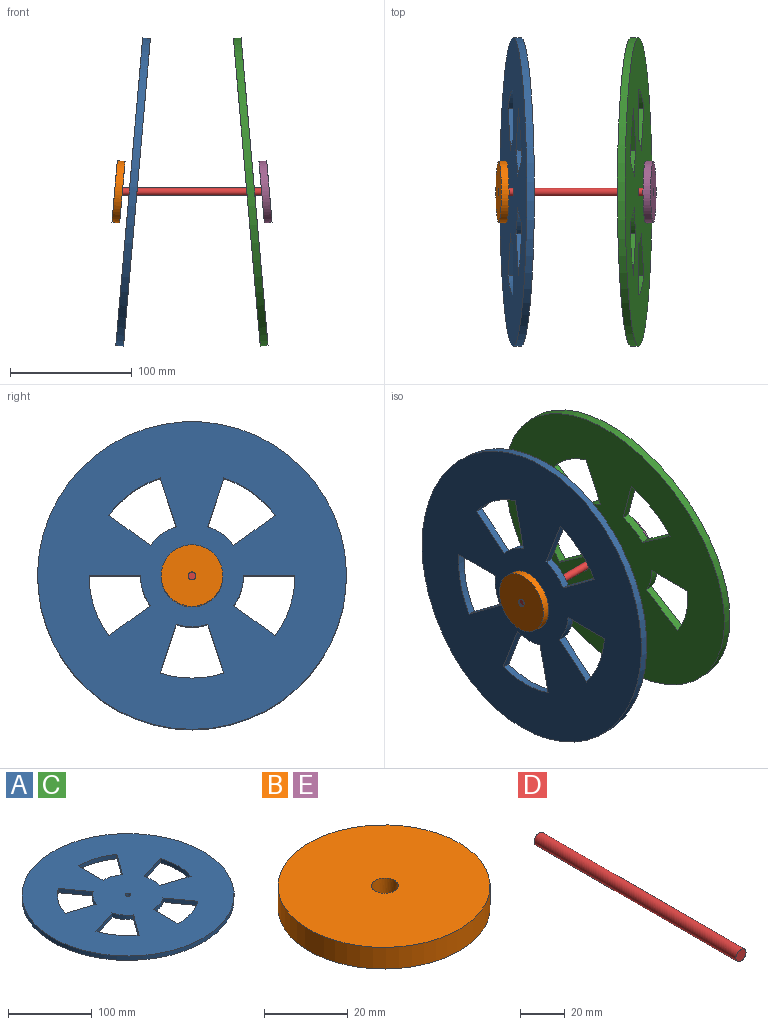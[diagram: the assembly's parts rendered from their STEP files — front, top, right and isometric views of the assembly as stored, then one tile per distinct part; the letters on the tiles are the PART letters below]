
ASSEMBLY  parts=5 mates=4
PART A: 24 faces, bbox 254x254x7.5 mm
  f0: plane 40.26x13.08mm, normal (0.31,0.95,0), area 268.8mm2, adj f1,f20,f21,f22
  f1: cylinder r=42.33mm len=26.16mm, axis (0,0,1), area 168.9mm2, adj f0,f2,f21,f22
  f2: plane 40.26x13.08mm, normal (0.31,-0.95,0), area 268.8mm2, adj f1,f20,f21,f22
  f3: plane 42.33x6.35mm, normal (1,0,0), area 268.8mm2, adj f4,f15,f21,f22
  f4: cylinder r=42.33mm len=24.88mm, axis (0,0,1), area 168.9mm2, adj f3,f5,f21,f22
  f5: plane 34.25x24.88mm, normal (-0.81,-0.59,0), area 268.8mm2, adj f4,f15,f21,f22
  f6: plane 40.26x13.08mm, normal (0.31,-0.95,0), area 268.8mm2, adj f7,f16,f21,f22
  f7: cylinder r=42.33mm len=21.17mm, axis (0,0,1), area 168.9mm2, adj f6,f8,f21,f22
  f8: plane 34.25x24.88mm, normal (-0.81,0.59,0), area 268.8mm2, adj f7,f16,f21,f22
  f9: plane 34.25x24.88mm, normal (-0.81,-0.59,0), area 268.8mm2, adj f10,f17,f21,f22
  f10: cylinder r=42.33mm len=21.17mm, axis (0,0,1), area 168.9mm2, adj f9,f11,f21,f22
  f11: plane 40.26x13.08mm, normal (0.31,0.95,0), area 268.8mm2, adj f10,f17,f21,f22
  f12: plane 42.33x6.35mm, normal (1,0,0), area 268.8mm2, adj f13,f19,f21,f22
  f13: cylinder r=84.67mm len=49.77mm, axis (0,0,1), area 337.8mm2, adj f12,f14,f21,f22
  f14: plane 34.25x24.88mm, normal (-0.81,0.59,0), area 268.8mm2, adj f13,f19,f21,f22
  f15: cylinder r=84.67mm len=49.77mm, axis (0,0,1), area 337.8mm2, adj f3,f5,f21,f22
  f16: cylinder r=84.67mm len=42.33mm, axis (0,0,1), area 337.8mm2, adj f6,f8,f21,f22
  f17: cylinder r=84.67mm len=42.33mm, axis (0,0,1), area 337.8mm2, adj f9,f11,f21,f22
  f18: cylinder r=127mm len=254mm, axis (0,0,1), area 5067.1mm2, adj f21,f22
  f19: cylinder r=42.33mm len=24.88mm, axis (0,0,1), area 168.9mm2, adj f12,f14,f21,f22
  f20: cylinder r=84.67mm len=52.33mm, axis (0,0,1), area 337.8mm2, adj f0,f2,f21,f22
  f21: plane 254x254mm, normal (0,0,-1), area 42193.8mm2, adj f0,f1,f2,f3,f4,f5,f6,f7
  f22: plane 254x254mm, normal (0,0,1), area 42193.8mm2, adj f0,f1,f2,f3,f4,f5,f6,f7
  f23: cylinder r=3.17mm len=7.46mm, axis (0.09,0,1), area 127.2mm2, adj f21,f22
PART B: 4 faces, bbox 50.8x50.8x7.5 mm
  f0: cylinder r=25.4mm len=50.8mm, axis (0,0,1), area 1013.4mm2, adj f1,f2
  f1: plane 50.8x50.8mm, normal (0,0,-1), area 1995mm2, adj f0,f3
  f2: plane 50.8x50.8mm, normal (0,0,1), area 1995mm2, adj f0,f3
  f3: cylinder r=3.17mm len=7.46mm, axis (0.09,0,1), area 127.2mm2, adj f1,f2
PART C: same geometry as A
PART D: 3 faces, bbox 6.4x127x6.4 mm
  f0: cylinder r=3.17mm len=127mm, axis (0,1,0), area 2533.5mm2, adj f1,f2
  f1: plane 6.35x6.35mm, normal (0,-1,0), area 31.7mm2, adj f0
  f2: plane 6.35x6.35mm, normal (0,1,0), area 31.7mm2, adj f0
PART E: same geometry as B
PLACE A rot(axis=(0.68,0,-0.74),180deg) t=(-45.06,0.17,0.21)mm
PLACE B rot(axis=(0.68,0,-0.74),180deg) t=(-57.08,0.17,0.21)mm
PLACE C rot(axis=(0,1,0),85deg) t=(51.63,0.17,0.21)mm
PLACE D rot(axis=(0.58,0.58,-0.58),120deg) t=(3.97,0.17,0.21)mm
PLACE E rot(axis=(0,1,0),85deg) t=(63.82,0.17,0.21)mm
MATE slider B.f3 <-> D.f0  axis (-1,0,0) through (-57.08,0.17,0.21)mm
MATE slider E.f3 <-> D.f0  axis (1,0,0) through (67.33,0.17,0.21)mm
MATE slider D.f0 <-> C.f23  axis (1,0,0) through (3.97,0.17,0.21)mm
MATE slider A.f23 <-> D.f0  axis (-1,0,0) through (-45.06,0.17,0.21)mm
